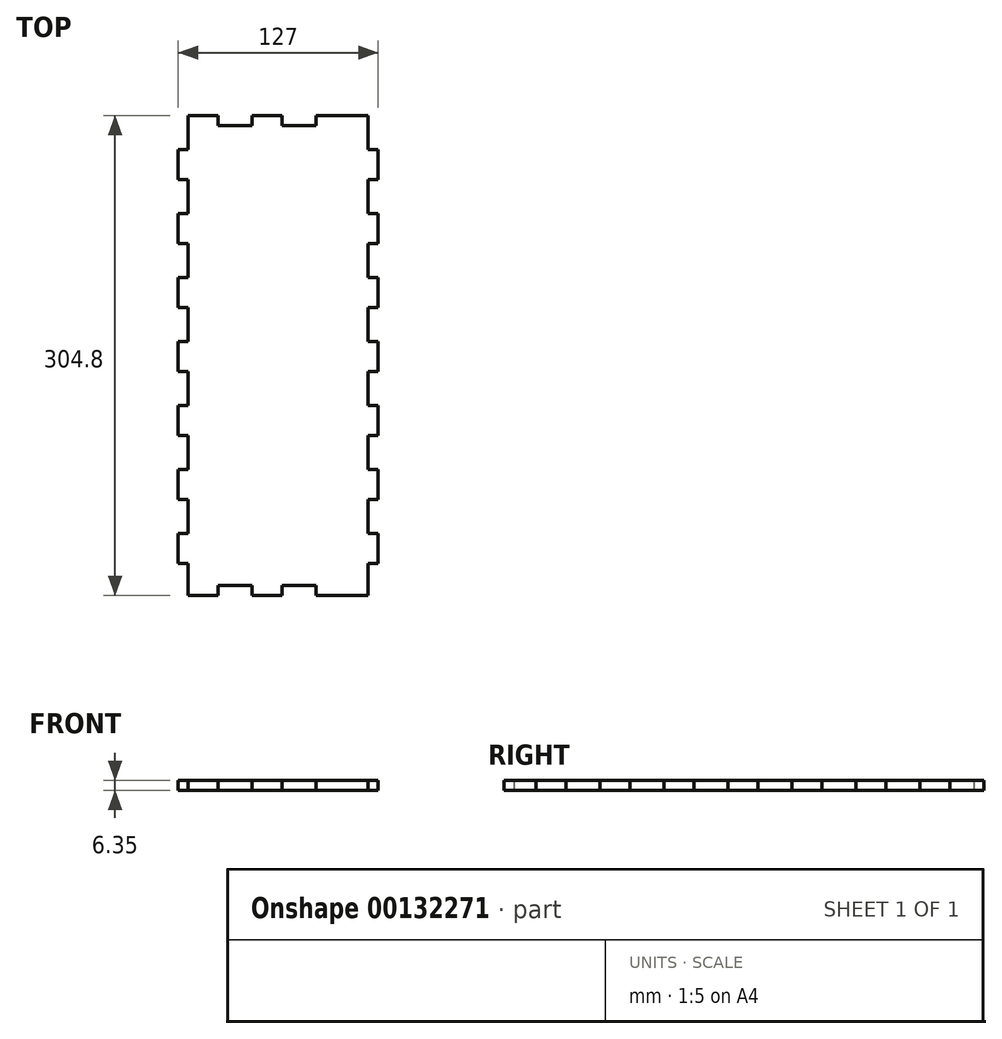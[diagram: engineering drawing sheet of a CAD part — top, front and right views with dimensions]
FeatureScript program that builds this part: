
annotation { "Feature Type Name" : "Feature", "Feature Type Description" : "" }
export const myFeature = defineFeature(function(context is Context, id is Id, definition is map)
    precondition{}
    {
        {
            var Q0;
            Q0=qCreatedBy(makeId("Top.planeOp"),FACE);
            var sketch = newSketch(context, id + "F0", { "sketchPlane" : qUnion([Q0])});
            skLineSegment(sketch, "E0.bottom", {"start": v(-76.2, 152.4) * mm, "end": v(63.5, 152.4) * mm, "construction": true});
            skLineSegment(sketch, "E0.top", {"start": v(-76.2, -152.4) * mm, "end": v(57.15, -152.4) * mm, "construction": true});
            skLineSegment(sketch, "E0.left", {"start": v(-76.2, 152.4) * mm, "end": v(-76.2, -152.4) * mm, "construction": true});
            skLineSegment(sketch, "E0.right", {"start": v(63.5, 152.4) * mm, "end": v(63.5, -152.4) * mm, "construction": true});
            skLineSegment(sketch, "E1", {"start": v(0, 114.14) * mm, "end": v(0, 0) * mm, "construction": true});
            skLineSegment(sketch, "E2", {"start": v(0, 0) * mm, "end": v(80.12, 0) * mm, "construction": true});
            skLineSegment(sketch, "E3", {"start": v(57.15, 152.4) * mm, "end": v(57.15, 130.81) * mm});
            skLineSegment(sketch, "E4", {"start": v(57.15, 130.8) * mm, "end": v(63.5, 130.8) * mm});
            skLineSegment(sketch, "E5", {"start": v(63.5, 130.81) * mm, "end": v(63.5, 111.76) * mm});
            skLineSegment(sketch, "E6", {"start": v(63.5, 111.76) * mm, "end": v(57.15, 111.76) * mm});
            skLineSegment(sketch, "E7.0.1.0", {"start": v(63.5, 90.17) * mm, "end": v(63.5, 71.12) * mm});
            skLineSegment(sketch, "E7.0.1.1", {"start": v(63.5, 71.12) * mm, "end": v(57.15, 71.12) * mm});
            skLineSegment(sketch, "E7.0.1.2", {"start": v(57.15, 90.17) * mm, "end": v(63.5, 90.17) * mm});
            skLineSegment(sketch, "E7.0.1.3", {"start": v(57.15, 111.76) * mm, "end": v(57.15, 90.17) * mm});
            skLineSegment(sketch, "E7.0.2.0", {"start": v(63.5, 49.53) * mm, "end": v(63.5, 30.48) * mm});
            skLineSegment(sketch, "E7.0.2.1", {"start": v(63.5, 30.48) * mm, "end": v(57.15, 30.48) * mm});
            skLineSegment(sketch, "E7.0.2.2", {"start": v(57.15, 49.53) * mm, "end": v(63.5, 49.53) * mm});
            skLineSegment(sketch, "E7.0.2.3", {"start": v(57.15, 71.12) * mm, "end": v(57.15, 49.53) * mm});
            skLineSegment(sketch, "E7.0.3.0", {"start": v(63.5, 8.9) * mm, "end": v(63.5, -10.16) * mm});
            skLineSegment(sketch, "E7.0.3.1", {"start": v(63.5, -10.16) * mm, "end": v(57.15, -10.16) * mm});
            skLineSegment(sketch, "E7.0.3.2", {"start": v(57.15, 8.89) * mm, "end": v(63.5, 8.89) * mm});
            skLineSegment(sketch, "E7.0.3.3", {"start": v(57.15, 30.48) * mm, "end": v(57.15, 8.9) * mm});
            skLineSegment(sketch, "E7.0.4.0", {"start": v(63.5, -31.75) * mm, "end": v(63.5, -50.8) * mm});
            skLineSegment(sketch, "E7.0.4.1", {"start": v(63.5, -50.8) * mm, "end": v(57.15, -50.8) * mm});
            skLineSegment(sketch, "E7.0.4.2", {"start": v(57.15, -31.75) * mm, "end": v(63.5, -31.75) * mm});
            skLineSegment(sketch, "E7.0.4.3", {"start": v(57.15, -10.16) * mm, "end": v(57.15, -31.75) * mm});
            skLineSegment(sketch, "E7.0.5.0", {"start": v(63.5, -72.39) * mm, "end": v(63.5, -91.44) * mm});
            skLineSegment(sketch, "E7.0.5.1", {"start": v(63.5, -91.44) * mm, "end": v(57.15, -91.44) * mm});
            skLineSegment(sketch, "E7.0.5.2", {"start": v(57.15, -72.4) * mm, "end": v(63.5, -72.4) * mm});
            skLineSegment(sketch, "E7.0.5.3", {"start": v(57.15, -50.8) * mm, "end": v(57.15, -72.39) * mm});
            skLineSegment(sketch, "E7.0.6.0", {"start": v(63.5, -113.03) * mm, "end": v(63.5, -132.08) * mm});
            skLineSegment(sketch, "E7.0.6.1", {"start": v(63.5, -132.08) * mm, "end": v(57.15, -132.08) * mm});
            skLineSegment(sketch, "E7.0.6.2", {"start": v(57.15, -113.03) * mm, "end": v(63.5, -113.03) * mm});
            skLineSegment(sketch, "E7.0.6.3", {"start": v(57.15, -91.44) * mm, "end": v(57.15, -113.03) * mm});
            skLineSegment(sketch, "E7.direction1", {"start": v(57.15, 111.76) * mm, "end": v(95.25, 111.76) * mm, "construction": true});
            skLineSegment(sketch, "E7.direction2", {"start": v(57.15, 111.76) * mm, "end": v(57.15, 71.12) * mm, "construction": true});
            skLineSegment(sketch, "E8", {"start": v(57.15, -132.08) * mm, "end": v(57.15, -152.4) * mm});
            skLineSegment(sketch, "E9.MirrorCS", {"start": v(-57.15, -113.03) * mm, "end": v(-63.5, -113.03) * mm});
            skLineSegment(sketch, "E10.MirrorCS", {"start": v(-57.15, -72.4) * mm, "end": v(-63.5, -72.4) * mm});
            skLineSegment(sketch, "E11.MirrorCS", {"start": v(-57.15, -31.75) * mm, "end": v(-63.5, -31.75) * mm});
            skLineSegment(sketch, "E12.MirrorCS", {"start": v(-63.5, -10.16) * mm, "end": v(-57.15, -10.16) * mm});
            skLineSegment(sketch, "E13.MirrorCS", {"start": v(-63.5, 30.48) * mm, "end": v(-57.15, 30.48) * mm});
            skLineSegment(sketch, "E14.MirrorCS", {"start": v(-57.15, 130.8) * mm, "end": v(-63.5, 130.8) * mm});
            skLineSegment(sketch, "E15.MirrorCS", {"start": v(-63.5, 71.12) * mm, "end": v(-57.15, 71.12) * mm});
            skLineSegment(sketch, "E16.MirrorCS", {"start": v(-57.15, 49.53) * mm, "end": v(-63.5, 49.53) * mm});
            skLineSegment(sketch, "E17.MirrorCS", {"start": v(-63.5, 111.76) * mm, "end": v(-57.15, 111.76) * mm});
            skLineSegment(sketch, "E18.MirrorCS", {"start": v(-63.5, -91.44) * mm, "end": v(-57.15, -91.44) * mm});
            skLineSegment(sketch, "E19.MirrorCS", {"start": v(-57.15, 90.17) * mm, "end": v(-63.5, 90.17) * mm});
            skLineSegment(sketch, "E20.MirrorCS", {"start": v(-63.5, -50.8) * mm, "end": v(-57.15, -50.8) * mm});
            skLineSegment(sketch, "E21.MirrorCS", {"start": v(-57.15, 8.89) * mm, "end": v(-63.5, 8.89) * mm});
            skLineSegment(sketch, "E22.MirrorCS", {"start": v(-63.5, -132.08) * mm, "end": v(-57.15, -132.08) * mm});
            skLineSegment(sketch, "E23.MirrorCS", {"start": v(-63.5, -72.39) * mm, "end": v(-63.5, -91.44) * mm});
            skLineSegment(sketch, "E24.MirrorCS", {"start": v(-57.15, 30.48) * mm, "end": v(-57.15, 8.9) * mm});
            skLineSegment(sketch, "E25.MirrorCS", {"start": v(-63.5, -113.03) * mm, "end": v(-63.5, -132.08) * mm});
            skLineSegment(sketch, "E26.MirrorCS", {"start": v(-63.5, 152.4) * mm, "end": v(-63.5, -152.4) * mm, "construction": true});
            skLineSegment(sketch, "E27.MirrorCS", {"start": v(-57.15, 111.76) * mm, "end": v(-57.15, 71.12) * mm, "construction": true});
            skLineSegment(sketch, "E28.MirrorCS", {"start": v(-57.15, 71.12) * mm, "end": v(-57.15, 49.53) * mm});
            skLineSegment(sketch, "E29.MirrorCS", {"start": v(-57.15, 111.76) * mm, "end": v(-57.15, 90.17) * mm});
            skLineSegment(sketch, "E30.MirrorCS", {"start": v(-63.5, 49.53) * mm, "end": v(-63.5, 30.48) * mm});
            skLineSegment(sketch, "E31.MirrorCS", {"start": v(-57.15, -91.44) * mm, "end": v(-57.15, -113.03) * mm});
            skLineSegment(sketch, "E32.MirrorCS", {"start": v(-57.15, 152.4) * mm, "end": v(-57.15, 130.8) * mm});
            skLineSegment(sketch, "E33.MirrorCS", {"start": v(-63.5, 90.17) * mm, "end": v(-63.5, 71.12) * mm});
            skLineSegment(sketch, "E34.MirrorCS", {"start": v(-57.15, -10.16) * mm, "end": v(-57.15, -31.75) * mm});
            skLineSegment(sketch, "E35.MirrorCS", {"start": v(-57.15, -132.08) * mm, "end": v(-57.15, -152.4) * mm});
            skLineSegment(sketch, "E36.MirrorCS", {"start": v(-63.5, 8.9) * mm, "end": v(-63.5, -10.16) * mm});
            skLineSegment(sketch, "E37.MirrorCS", {"start": v(-57.15, -50.8) * mm, "end": v(-57.15, -72.39) * mm});
            skLineSegment(sketch, "E38.MirrorCS", {"start": v(-63.5, 130.81) * mm, "end": v(-63.5, 111.76) * mm});
            skLineSegment(sketch, "E39.MirrorCS", {"start": v(-63.5, -31.75) * mm, "end": v(-63.5, -50.8) * mm});
            skLineSegment(sketch, "E40", {"start": v(-57.15, 152.4) * mm, "end": v(-38.1, 152.4) * mm});
            skLineSegment(sketch, "E41", {"start": v(-38.1, 152.4) * mm, "end": v(-38.1, 146.05) * mm});
            skLineSegment(sketch, "E42", {"start": v(-38.1, 146.05) * mm, "end": v(-16.51, 146.05) * mm});
            skLineSegment(sketch, "E43", {"start": v(-16.51, 146.05) * mm, "end": v(-16.51, 152.4) * mm});
            skLineSegment(sketch, "E44.1.0.0", {"start": v(2.54, 152.4) * mm, "end": v(2.54, 146.05) * mm});
            skLineSegment(sketch, "E44.1.0.1", {"start": v(2.54, 146.05) * mm, "end": v(24.13, 146.05) * mm});
            skLineSegment(sketch, "E44.1.0.2", {"start": v(-16.51, 152.4) * mm, "end": v(2.54, 152.4) * mm});
            skLineSegment(sketch, "E44.1.0.3", {"start": v(24.13, 146.05) * mm, "end": v(24.13, 152.4) * mm});
            skLineSegment(sketch, "E44.direction1", {"start": v(-57.15, 152.4) * mm, "end": v(-16.51, 152.4) * mm, "construction": true});
            skLineSegment(sketch, "E45", {"start": v(64.77, 152.4) * mm, "end": v(57.15, 152.4) * mm});
            skLineSegment(sketch, "E46.MirrorCS", {"start": v(24.13, -146.05) * mm, "end": v(24.13, -152.4) * mm});
            skLineSegment(sketch, "E47.MirrorCS", {"start": v(-16.5, -146.05) * mm, "end": v(-16.5, -152.4) * mm});
            skLineSegment(sketch, "E48.MirrorCS", {"start": v(2.54, -152.4) * mm, "end": v(2.54, -146.05) * mm});
            skLineSegment(sketch, "E49.MirrorCS", {"start": v(-38.1, -152.4) * mm, "end": v(-38.1, -146.05) * mm});
            skLineSegment(sketch, "E50.MirrorCS", {"start": v(-57.15, -152.4) * mm, "end": v(-38.1, -152.4) * mm});
            skLineSegment(sketch, "E51.MirrorCS", {"start": v(-57.15, -152.4) * mm, "end": v(-16.5, -152.4) * mm, "construction": true});
            skLineSegment(sketch, "E52.MirrorCS", {"start": v(-16.5, -152.4) * mm, "end": v(2.54, -152.4) * mm});
            skLineSegment(sketch, "E53.MirrorCS", {"start": v(-38.1, -146.05) * mm, "end": v(-16.5, -146.05) * mm});
            skLineSegment(sketch, "E54.MirrorCS", {"start": v(24.13, -152.4) * mm, "end": v(43.18, -152.4) * mm});
            skLineSegment(sketch, "E55.MirrorCS", {"start": v(2.54, -146.05) * mm, "end": v(24.13, -146.05) * mm});
            skLineSegment(sketch, "E56", {"start": v(24.13, 152.4) * mm, "end": v(57.15, 152.4) * mm});
            skLineSegment(sketch, "E57", {"start": v(43.18, -152.4) * mm, "end": v(57.15, -152.4) * mm});
            skSolve(sketch);
        }
        {
            var Q0;
            Q0=makeQuery(id+"F0.imprint","IMPRINT",FACE,{"disambiguationData":[TD([[makeQuery(id+"F0.imprint","IMPRINT",EDGE,{"derivedFrom":sQuery(id+"F0.wireOp",EDGE,"E3")}),-1.0]])]});
            extrude(context, id + "F1", {"entities" : qUnion([Q0]), "depth" : 6.35 * mm});
        }
    });
